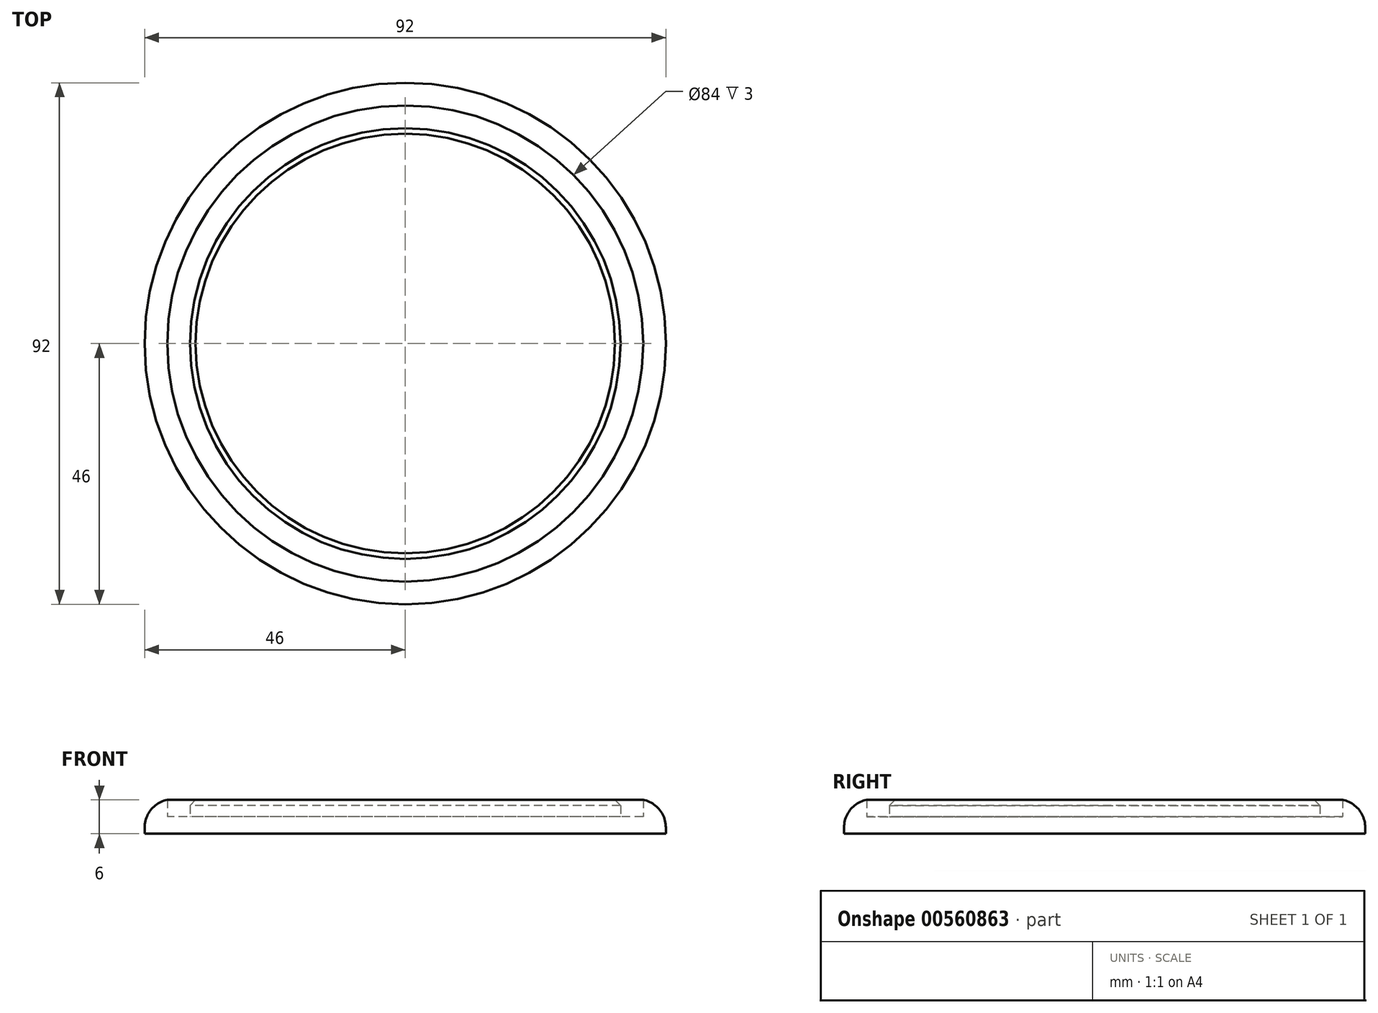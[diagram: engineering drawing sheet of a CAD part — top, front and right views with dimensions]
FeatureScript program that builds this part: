
annotation { "Feature Type Name" : "Feature", "Feature Type Description" : "" }
export const myFeature = defineFeature(function(context is Context, id is Id, definition is map)
    precondition{}
    {
        {
            var Q0;
            Q0=qCreatedBy(makeId("Top.planeOp"),FACE);
            var sketch = newSketch(context, id + "F0", { "sketchPlane" : qUnion([Q0])});
            skCircle(sketch, "E0", {"center": v(0, 0) * mm, "radius": 38 * mm});
            skCircle(sketch, "E1", {"center": v(0, 0) * mm, "radius": 42 * mm});
            skCircle(sketch, "E2", {"center": v(0, 0) * mm, "radius": 46 * mm});
            skSolve(sketch);
        }
        {
            var Q0;
            Q0=makeQuery(id+"F0.imprint","IMPRINT",FACE,{"disambiguationData":[TD([[makeQuery(id+"F0.imprint","IMPRINT",EDGE,{"derivedFrom":sQuery(id+"F0.wireOp",EDGE,"E0")}),1.0]])]});
            var Q1;
            Q1=makeQuery(id+"F0.imprint","IMPRINT",FACE,{"disambiguationData":[TD([[makeQuery(id+"F0.imprint","IMPRINT",EDGE,{"derivedFrom":sQuery(id+"F0.wireOp",EDGE,"E0")}),-1.0]])]});
            var Q2;
            Q2=makeQuery(id+"F0.imprint","IMPRINT",FACE,{"disambiguationData":[TD([[makeQuery(id+"F0.imprint","IMPRINT",EDGE,{"derivedFrom":sQuery(id+"F0.wireOp",EDGE,"E1")}),-1.0]])]});
            extrude(context, id + "F1", {"entities" : qUnion([Q0, Q1, Q2]), "depth" : 3 * mm, "offsetDistance" : 25 * mm});
        }
        {
            var Q0;
            Q0=makeQuery(id+"F0.imprint","IMPRINT",FACE,{"disambiguationData":[TD([[makeQuery(id+"F0.imprint","IMPRINT",EDGE,{"derivedFrom":sQuery(id+"F0.wireOp",EDGE,"E0")}),1.0]])]});
            var Q1;
            Q1=makeQuery(id+"F0.imprint","IMPRINT",FACE,{"disambiguationData":[TD([[makeQuery(id+"F0.imprint","IMPRINT",EDGE,{"derivedFrom":sQuery(id+"F0.wireOp",EDGE,"E1")}),-1.0]])]});
            extrude(context, id + "F2", {"entities" : qUnion([Q0, Q1]), "operationType" : NewBodyOperationType.ADD, "depth" : 6 * mm, "offsetDistance" : 25 * mm});
        }
        {
            var Q0;
            Q0=makeQuery(id+"F2.opExtrude","CAP_EDGE",EDGE,{"disambiguationData":[OSD([sQuery(id+"F0.wireOp",EDGE,"E2")])],"isStart":false});
            fillet(context, id + "F3", {"entities" : qUnion([Q0]), "radius" : 5 * mm, "tangentPropagation" : true, "allowEdgeOverflow" : false});
        }
        {
            var Q0;
            Q0=makeQuery(id+"F2.opExtrude","CAP_EDGE",EDGE,{"disambiguationData":[OSD([sQuery(id+"F0.wireOp",EDGE,"E0")])],"isStart":false});
            chamfer(context, id + "F4", {"entities" : qUnion([Q0]), "width" : 1 * mm, "tangentPropagation" : true});
        }
    });
